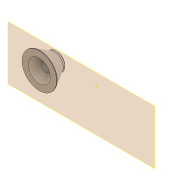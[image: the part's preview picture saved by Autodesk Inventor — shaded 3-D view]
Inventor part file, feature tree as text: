
AUTODESK INVENTOR PART (.ipt)
format: ipt  version: 2021 (Build 250183000, 183)  size: 121,856 bytes
history: native  units: mm
features: sketch x4, chamfer x3, extrude x2, projected_geometry x2, other x2, plane x1, hole x1, fillet x1, reference x1
ambient origin geometry x8: Origin, YZ Plane, XZ Plane, XY Plane, X Axis, Y Axis, Z Axis, Center Point
bodies: Solid1 (feature_tree)
feature tree (17):
  plane  "Work Plane1"
  extrude  "Extrusion1"  Depth=9.5mm
  sketch  "Sketch2"  dims[d3=1.5mm d4=0.0mm]
  extrude  "Extrusion2"  Depth=0.5mm TaperAngle=45.0deg
  hole  "Hole1"  [1 undecoded]
  chamfer  "Chamfer1"  Distance=0.4mm
  chamfer  "Chamfer2"  [1 undecoded]
  chamfer  "Chamfer3"  [1 undecoded]
  fillet  "Fillet1"  [1 undecoded]
  sketch  "Sketch1"  dims[d0=22.3mm d1=9.5mm d2=-5.235988mm]
  reference  "Reference1"
  sketch  "Sketch3"  dims[d5=5.5mm d6=6.0mm d7=13.9mm d8=2.0mm d9=90.0deg d10=37.0mm d11=20.594885mm d12=0.5mm d13=2.0mm d14=45.0deg]
  projected_geometry  "Projected Loop1"
  sketch  "Sketch4"  dims[d15=0.5mm d16=2.0mm d17=45.0deg d18=0.25mm d19=2.0mm d20=14.835299mm d21=0.4mm]
  projected_geometry  "Projected Loop2"
  other  "Assembly2"
  other  "Wall Side:1"
note: 4 required parameter values undecoded (feature->parameter linkage not recoverable at this tier; creation-order binding heuristic only, values carry confidence <= 0.55)
